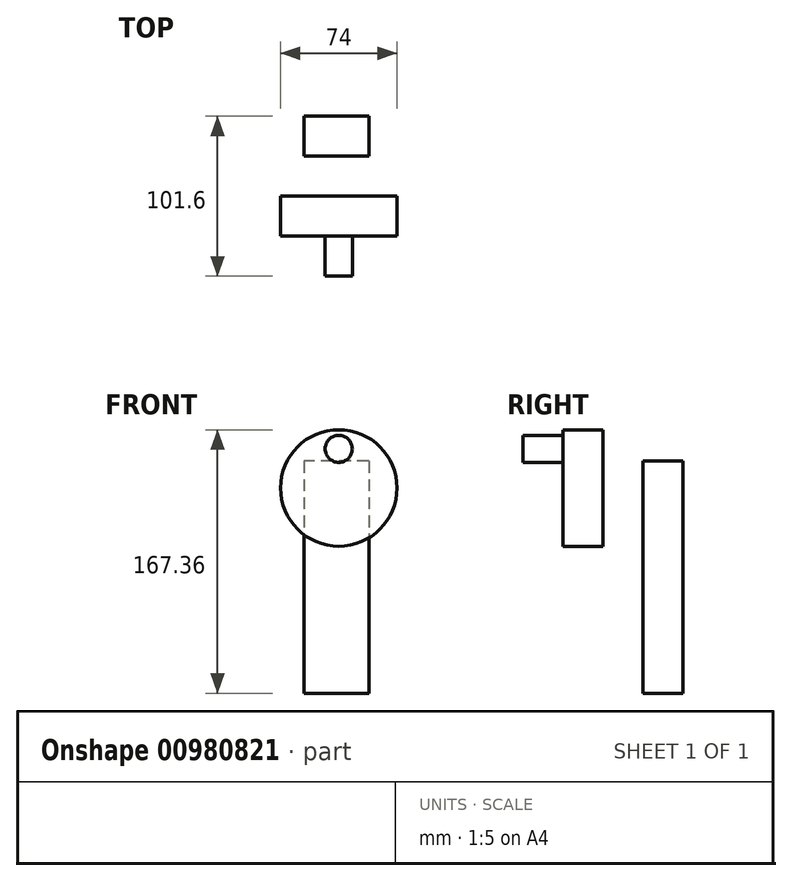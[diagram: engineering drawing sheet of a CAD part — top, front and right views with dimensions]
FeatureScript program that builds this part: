
annotation { "Feature Type Name" : "Feature", "Feature Type Description" : "" }
export const myFeature = defineFeature(function(context is Context, id is Id, definition is map)
    precondition{}
    {
        {
            var Q0;
            Q0=qCreatedBy(makeId("Front.planeOp"),FACE);
            var sketch = newSketch(context, id + "F0", { "sketchPlane" : qUnion([Q0])});
            skCircle(sketch, "E0", {"center": v(0, 0) * mm, "radius": 37 * mm});
            skSolve(sketch);
        }
        {
            var Q0;
            Q0=makeQuery(id+"F0.imprint","IMPRINT",FACE,{"disambiguationData":[TD([[makeQuery(id+"F0.imprint","IMPRINT",EDGE,{"derivedFrom":sQuery(id+"F0.wireOp",EDGE,"E0")}),1.0]])]});
            extrude(context, id + "F1", {"entities" : qUnion([Q0]), "depth" : 25.4 * mm, "offsetDistance" : 25.4 * mm});
        }
        {
            var Q0;
            Q0=makeQuery(id+"F1.opExtrude","CAP_FACE",FACE,{"disambiguationData":[OSD([sQuery(id+"F0.wireOp",EDGE,"E0")])],"isStart":false});
            var sketch = newSketch(context, id + "F2", { "sketchPlane" : qUnion([Q0])});
            skCircle(sketch, "E1", {"center": v(0, 24.89) * mm, "radius": 8.61 * mm});
            skSolve(sketch);
        }
        {
            var Q0;
            Q0=makeQuery(id+"F2.imprint","IMPRINT",FACE,{"disambiguationData":[TD([[makeQuery(id+"F2.imprint","IMPRINT",EDGE,{"derivedFrom":sQuery(id+"F2.wireOp",EDGE,"E1")}),1.0]])]});
            extrude(context, id + "F3", {"entities" : qUnion([Q0]), "operationType" : NewBodyOperationType.ADD, "depth" : 25.4 * mm, "offsetDistance" : 25.4 * mm});
        }
        {
            var Q0;
            Q0=qCreatedBy(makeId("Front.planeOp"),FACE);
            cPlane(context, id + "F4", {"entities" : qUnion([Q0]), "cplaneType" : CPlaneType.OFFSET, "offset" : 25.4 * mm, "oppositeDirection" : true, "width" : 152.4 * mm, "height" : 152.4 * mm});
        }
        {
            var Q0;
            Q0=qCreatedBy(id+"F4.planeOp",FACE);
            var sketch = newSketch(context, id + "F5", { "sketchPlane" : qUnion([Q0])});
            skLineSegment(sketch, "E2.bottom", {"start": v(19.12, 17.03) * mm, "end": v(-22.1, 17.03) * mm});
            skLineSegment(sketch, "E2.top", {"start": v(19.12, -130.36) * mm, "end": v(-22.1, -130.36) * mm});
            skLineSegment(sketch, "E2.left", {"start": v(19.12, 17.03) * mm, "end": v(19.12, -130.36) * mm});
            skLineSegment(sketch, "E2.right", {"start": v(-22.1, 17.03) * mm, "end": v(-22.1, -130.36) * mm});
            skSolve(sketch);
        }
        {
            var Q0;
            Q0=makeQuery(id+"F5.imprint","IMPRINT",FACE,{"disambiguationData":[TD([[makeQuery(id+"F5.imprint","IMPRINT",EDGE,{"derivedFrom":sQuery(id+"F5.wireOp",EDGE,"E2.bottom")}),1.0]])]});
            extrude(context, id + "F6", {"entities" : qUnion([Q0]), "oppositeDirection" : true, "depth" : 25.4 * mm, "offsetDistance" : 25.4 * mm});
        }
    });
